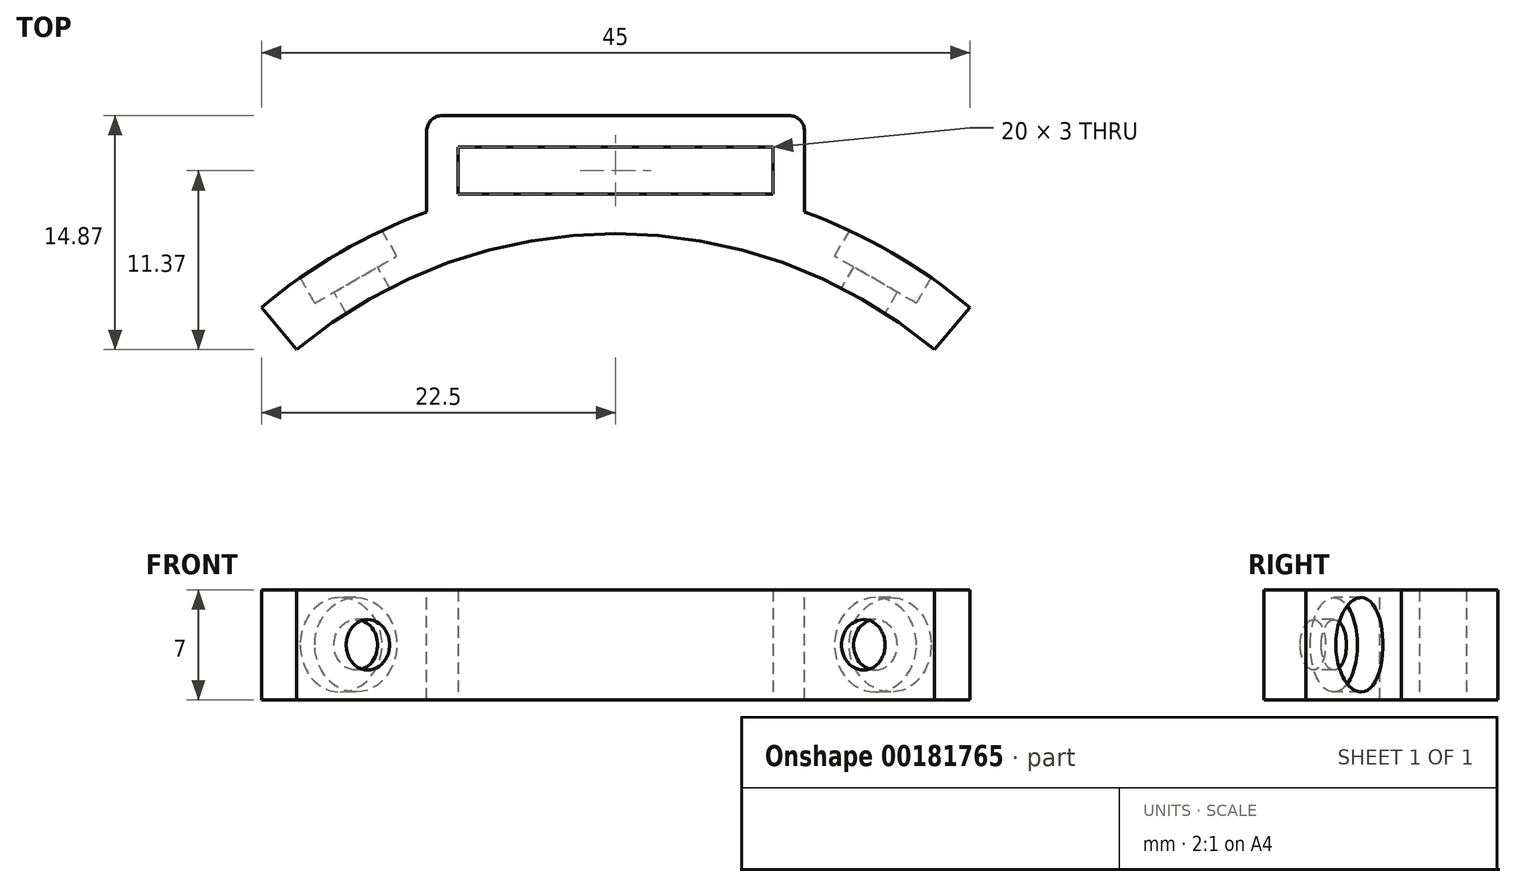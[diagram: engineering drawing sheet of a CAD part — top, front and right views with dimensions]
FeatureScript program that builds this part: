
annotation { "Feature Type Name" : "Feature", "Feature Type Description" : "" }
export const myFeature = defineFeature(function(context is Context, id is Id, definition is map)
    precondition{}
    {
        {
            var Q0;
            Q0=qCreatedBy(makeId("Top.planeOp"),FACE);
            var sketch = newSketch(context, id + "F0", { "sketchPlane" : qUnion([Q0])});
            skCircle(sketch, "E0", {"center": v(0, 0) * mm, "radius": 31.5 * mm});
            skCircle(sketch, "E1", {"center": v(0, 0) * mm, "radius": 35 * mm});
            skSolve(sketch);
        }
        {
            var Q0;
            Q0 = qSketchRegion(id + "F0", true);
            var Q1;
            Q1=sQuery(id+"F0.wireOp",EDGE,"E1");
            extrude(context, id + "F1", {"entities" : qUnion([Q0]), "surfaceEntities" : qUnion([Q1]), "endBound" : BoundingType.SYMMETRIC, "oppositeDirection" : true, "depth" : 7 * mm});
        }
        {
            var Q0;
            Q0=qCreatedBy(makeId("Top.planeOp"),FACE);
            var sketch = newSketch(context, id + "F2", { "sketchPlane" : qUnion([Q0])});
            skLineSegment(sketch, "E2.bottom", {"start": v(11, 39) * mm, "end": v(-11, 39) * mm});
            skLineSegment(sketch, "E2.top", {"start": v(12, 31.5) * mm, "end": v(-12, 31.5) * mm});
            skLineSegment(sketch, "E2.left", {"start": v(12, 38) * mm, "end": v(12, 31.5) * mm});
            skLineSegment(sketch, "E2.right", {"start": v(-12, 38) * mm, "end": v(-12, 31.5) * mm});
            skLineSegment(sketch, "E3.bottom", {"start": v(-10, 37) * mm, "end": v(10, 37) * mm});
            skLineSegment(sketch, "E3.top", {"start": v(-10, 34) * mm, "end": v(10, 34) * mm});
            skLineSegment(sketch, "E3.left", {"start": v(-10, 37) * mm, "end": v(-10, 34) * mm});
            skLineSegment(sketch, "E3.right", {"start": v(10, 37) * mm, "end": v(10, 34) * mm});
            skPoint(sketch, "E4.visualSharp", {"position": v(-12, 39) * mm});
            skArc(sketch, "E4.filletArc", {"start": v(-11, 39) * mm, "mid": v(-11.7, 38.7) * mm, "end": v(-12, 38) * mm});
            skPoint(sketch, "E5.visualSharp", {"position": v(12, 39) * mm});
            skArc(sketch, "E5.filletArc", {"start": v(12, 38) * mm, "mid": v(11.7, 38.7) * mm, "end": v(11, 39) * mm});
            skSolve(sketch);
        }
        {
            var Q0;
            Q0=makeQuery(id+"F2.imprint","IMPRINT",FACE,{"disambiguationData":[TD([[makeQuery(id+"F2.imprint","IMPRINT",EDGE,{"derivedFrom":sQuery(id+"F2.wireOp",EDGE,"E2.bottom")}),1.0]])]});
            var Q1;
            Q1 = qSketchRegion(id + "F5", true);
            extrude(context, id + "F3", {"entities" : qUnion([Q0, Q1]), "operationType" : NewBodyOperationType.ADD, "endBound" : BoundingType.SYMMETRIC, "depth" : 7 * mm});
        }
        {
            var Q0;
            Q0=makeQuery(id+"F2.imprint","IMPRINT",FACE,{"disambiguationData":[TD([[makeQuery(id+"F2.imprint","IMPRINT",EDGE,{"derivedFrom":sQuery(id+"F2.wireOp",EDGE,"E3.bottom")}),-1.0]])]});
            extrude(context, id + "F4", {"entities" : qUnion([Q0]), "operationType" : NewBodyOperationType.REMOVE, "endBound" : BoundingType.SYMMETRIC, "oppositeDirection" : true, "depth" : 25 * mm});
        }
        {
            var Q0;
            Q0=qCreatedBy(makeId("Top.planeOp"),FACE);
            var sketch = newSketch(context, id + "F5", { "sketchPlane" : qUnion([Q0])});
            skLineSegment(sketch, "E6", {"start": v(0, 0) * mm, "end": v(30.06, 52.07) * mm, "construction": true});
            skLineSegment(sketch, "E7.bottom", {"start": v(17.89, 27.78) * mm, "end": v(16.5, 28.58) * mm});
            skLineSegment(sketch, "E7.top", {"start": v(16.1, 24.67) * mm, "end": v(14.7, 25.47) * mm});
            skLineSegment(sketch, "E7.left", {"start": v(17.89, 27.78) * mm, "end": v(16.1, 24.67) * mm});
            skLineSegment(sketch, "E7.right", {"start": v(16.5, 28.58) * mm, "end": v(14.7, 25.47) * mm});
            skCircle(sketch, "E8", {"center": v(0, 0) * mm, "radius": 33 * mm, "construction": true});
            skLineSegment(sketch, "E9.bottom", {"start": v(16.5, 28.58) * mm, "end": v(19.1, 27.08) * mm});
            skLineSegment(sketch, "E9.top", {"start": v(18.16, 31.46) * mm, "end": v(20.76, 29.96) * mm});
            skLineSegment(sketch, "E9.left", {"start": v(16.5, 28.58) * mm, "end": v(18.16, 31.46) * mm});
            skLineSegment(sketch, "E9.right", {"start": v(19.1, 27.08) * mm, "end": v(20.76, 29.96) * mm});
            skSolve(sketch);
        }
        {
            var Q0;
            Q0=qCreatedBy(makeId("Top.planeOp"),FACE);
            var sketch = newSketch(context, id + "F6", { "sketchPlane" : qUnion([Q0])});
            skLineSegment(sketch, "E10", {"start": v(0, 0) * mm, "end": v(-27.34, 47.35) * mm, "construction": true});
            skLineSegment(sketch, "E11.bottom", {"start": v(-17.89, 27.78) * mm, "end": v(-16.5, 28.58) * mm});
            skLineSegment(sketch, "E11.top", {"start": v(-16.1, 24.7) * mm, "end": v(-14.72, 25.5) * mm});
            skLineSegment(sketch, "E11.left", {"start": v(-17.89, 27.78) * mm, "end": v(-16.1, 24.7) * mm});
            skLineSegment(sketch, "E11.right", {"start": v(-16.5, 28.58) * mm, "end": v(-14.72, 25.5) * mm});
            skCircle(sketch, "E12", {"center": v(0, 0) * mm, "radius": 33 * mm, "construction": true});
            skLineSegment(sketch, "E13.bottom", {"start": v(-16.5, 28.58) * mm, "end": v(-19.1, 27.08) * mm});
            skLineSegment(sketch, "E13.top", {"start": v(-17.83, 30.88) * mm, "end": v(-20.43, 29.38) * mm});
            skLineSegment(sketch, "E13.left", {"start": v(-16.5, 28.58) * mm, "end": v(-17.83, 30.88) * mm});
            skLineSegment(sketch, "E13.right", {"start": v(-19.1, 27.08) * mm, "end": v(-20.43, 29.38) * mm});
            skSolve(sketch);
        }
        {
            var Q0;
            Q0=qCreatedBy(makeId("Top.planeOp"),FACE);
            var sketch = newSketch(context, id + "F7", { "sketchPlane" : qUnion([Q0])});
            skLineSegment(sketch, "E14", {"start": v(0, 0) * mm, "end": v(34.84, 41.52) * mm, "construction": true});
            skSolve(sketch);
        }
        {
            var Q0;
            Q0=sQuery(id+"F7.wireOp",EDGE,"E14");
            cPlane(context, id + "F8", {"entities" : qUnion([Q0]), "cplaneType" : CPlaneType.LINE_ANGLE, "offset" : 25 * mm, "angle" : 90 * degree, "width" : 150 * mm, "height" : 150 * mm});
        }
        {
            var Q0;
            Q0=qCreatedBy(id+"F8.planeOp",FACE);
            var sketch = newSketch(context, id + "F9", { "sketchPlane" : qUnion([Q0])});
            skLineSegment(sketch, "E15.bottom", {"start": v(27.94, 4.32) * mm, "end": v(38.42, 4.32) * mm});
            skLineSegment(sketch, "E15.top", {"start": v(27.94, -5.12) * mm, "end": v(38.42, -5.12) * mm});
            skLineSegment(sketch, "E15.left", {"start": v(27.94, 4.32) * mm, "end": v(27.94, -5.12) * mm});
            skLineSegment(sketch, "E15.right", {"start": v(38.42, 4.32) * mm, "end": v(38.42, -5.12) * mm});
            skLineSegment(sketch, "E16", {"start": v(0, 15.27) * mm, "end": v(0, -15.27) * mm});
            skSolve(sketch);
        }
        {
            var Q0;
            Q0=makeQuery(id+"F9.imprint","IMPRINT",FACE,{"disambiguationData":[TD([[makeQuery(id+"F9.imprint","IMPRINT",EDGE,{"derivedFrom":sQuery(id+"F9.wireOp",EDGE,"E15.bottom")}),-1.0]])]});
            var Q1;
            Q1=sQuery(id+"F9.wireOp",EDGE,"E16");
            revolve(context, id + "F10", {"operationType" : NewBodyOperationType.REMOVE, "entities" : qUnion([Q0]), "axis" : qUnion([Q1]), "revolveType" : RevolveType.ONE_DIRECTION, "angle" : 280 * degree});
        }
        {
            var Q0;
            Q0=makeQuery(id+"F5.imprint","IMPRINT",FACE,{"disambiguationData":[TD([[makeQuery(id+"F5.imprint","IMPRINT",EDGE,{"derivedFrom":sQuery(id+"F5.wireOp",EDGE,"E9.top")}),-1.0]])]});
            var Q1;
            Q1=makeQuery(id+"F5.imprint","IMPRINT",FACE,{"disambiguationData":[TD([[makeQuery(id+"F5.imprint","IMPRINT",EDGE,{"derivedFrom":sQuery(id+"F5.wireOp",EDGE,"E7.top")}),-1.0]])]});
            var Q2;
            Q2=sQuery(id+"F5.wireOp",EDGE,"E6");
            revolve(context, id + "F11", {"operationType" : NewBodyOperationType.REMOVE, "entities" : qUnion([Q0, Q1]), "axis" : qUnion([Q2]), "revolveType" : RevolveType.FULL});
        }
        {
            var Q0;
            Q0 = qSketchRegion(id + "F6", true);
            var Q1;
            Q1=sQuery(id+"F6.wireOp",EDGE,"E10");
            revolve(context, id + "F12", {"operationType" : NewBodyOperationType.REMOVE, "entities" : qUnion([Q0]), "axis" : qUnion([Q1]), "revolveType" : RevolveType.FULL, "oppositeDirection" : true});
        }
    });
